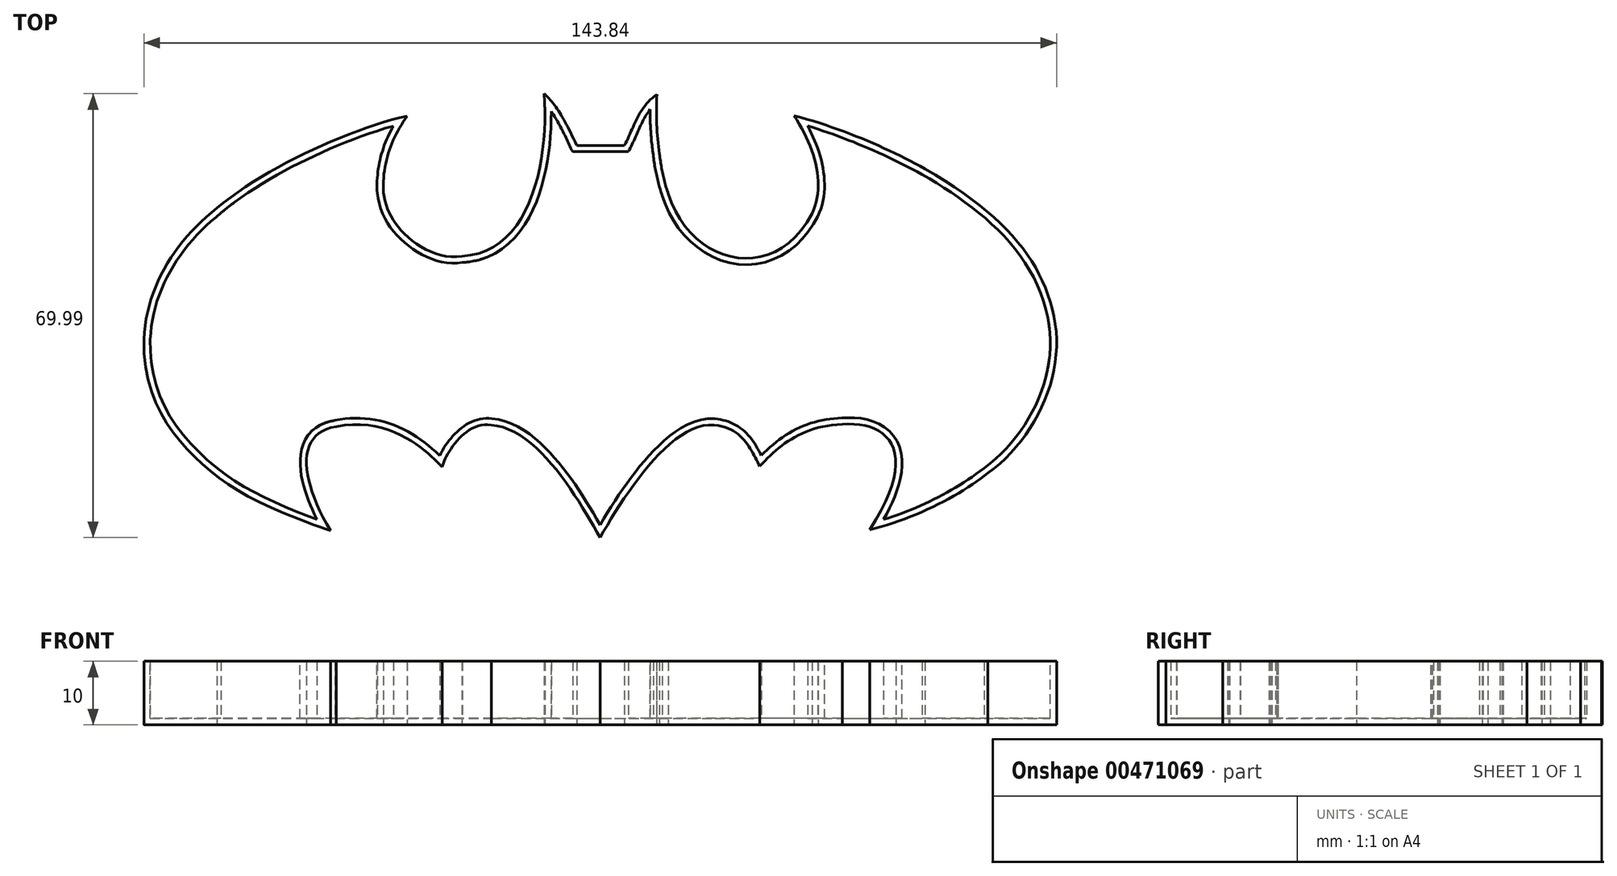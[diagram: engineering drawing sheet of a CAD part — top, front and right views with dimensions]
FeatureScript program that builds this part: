
annotation { "Feature Type Name" : "Feature", "Feature Type Description" : "" }
export const myFeature = defineFeature(function(context is Context, id is Id, definition is map)
    precondition{}
    {
        {
            var Q0;
            Q0=qCreatedBy(makeId("Top.planeOp"),FACE);
            var sketch = newSketch(context, id + "F0", { "sketchPlane" : qUnion([Q0])});
            skLineSegment(sketch, "E0", {"start": v(-3.19, 26.94) * mm, "end": v(4.35, 26.94) * mm});
            skFitSpline(sketch, "E1", {"points": [v(-3.19, 26.94) * mm, v(-8.28, 35.1) * mm], "startDerivative": vector(-5.79, 12.5) * mm, "endDerivative": vector(-5.83, 5.43) * mm});
            skFitSpline(sketch, "E2", {"points": [v(-8.28, 35.1) * mm, v(-21.29, 9.5) * mm], "startDerivative": vector(2.01, -31.97) * mm, "endDerivative": vector(-32.77, -1.6) * mm});
            skFitSpline(sketch, "E3", {"points": [v(-21.29, 9.5) * mm, v(-30.65, 13.35) * mm, v(-33.63, 19.52) * mm], "startDerivative": vector(-19.33, -3.63) * mm, "endDerivative": vector(-2.12, 15.56) * mm});
            skFitSpline(sketch, "E4", {"points": [v(-33.63, 19.52) * mm, v(-29.9, 31.6) * mm], "startDerivative": vector(-0.8, 13.72) * mm, "endDerivative": vector(7.34, 10.53) * mm});
            skFitSpline(sketch, "E5", {"points": [v(-29.9, 31.6) * mm, v(-59.86, 17.08) * mm], "startDerivative": vector(-27.2, -6.27) * mm, "endDerivative": vector(-23.05, -19.48) * mm});
            skFitSpline(sketch, "E6", {"points": [v(-59.86, 17.08) * mm, v(-71.38, -3.61) * mm], "startDerivative": vector(-19.7, -15.69) * mm, "endDerivative": vector(-1.19, -25.13) * mm});
            skFitSpline(sketch, "E7", {"points": [v(-71.38, -3.61) * mm, v(-63.46, -22.06) * mm, v(-41.97, -33.78) * mm], "startDerivative": vector(-1.21, -53.46) * mm, "endDerivative": vector(62.7, -21.26) * mm});
            skFitSpline(sketch, "E8", {"points": [v(-41.97, -33.78) * mm, v(-41.08, -17.39) * mm], "startDerivative": vector(-14.53, 24.29) * mm, "endDerivative": vector(19.35, 2.83) * mm});
            skFitSpline(sketch, "E9", {"points": [v(-41.08, -17.39) * mm, v(-24.7, -23.4) * mm, v(-24.4, -23.76) * mm], "startDerivative": vector(31.3, 6.7) * mm, "endDerivative": vector(-0.55, -1.09) * mm});
            skFitSpline(sketch, "E10", {"points": [v(-24.4, -23.76) * mm, v(-16.64, -17.13) * mm], "startDerivative": vector(1.48, 5.94) * mm, "endDerivative": vector(12.45, -2) * mm});
            skFitSpline(sketch, "E11", {"points": [v(-16.64, -17.13) * mm, v(0.5, -34.88) * mm], "startDerivative": vector(21.55, -1.44) * mm, "endDerivative": vector(11.01, -19.55) * mm});
            skFitSpline(sketch, "E12", {"points": [v(0.5, -34.88) * mm, v(18.52, -17.15) * mm], "startDerivative": vector(12.1, 21.48) * mm, "endDerivative": vector(19.7, -2.01) * mm});
            skFitSpline(sketch, "E13", {"points": [v(18.52, -17.15) * mm, v(25.67, -23.64) * mm], "startDerivative": vector(13.77, -1.3) * mm, "endDerivative": vector(4.03, -7.43) * mm});
            skFitSpline(sketch, "E14", {"points": [v(38.66, -17.02) * mm, v(42.98, -33.64) * mm], "startDerivative": vector(21.92, 1.91) * mm, "endDerivative": vector(-24.23, -36.8) * mm});
            skFitSpline(sketch, "E15", {"points": [v(38.66, -17.02) * mm, v(25.67, -23.64) * mm], "startDerivative": vector(-19.1, -0.7) * mm, "endDerivative": vector(-9.1, -9.92) * mm});
            skFitSpline(sketch, "E16", {"points": [v(42.98, -33.64) * mm, v(61.62, -24.7) * mm], "startDerivative": vector(21.12, 4.96) * mm, "endDerivative": vector(12.58, 10.1) * mm});
            skFitSpline(sketch, "E17", {"points": [v(61.62, -24.7) * mm, v(72.02, 0) * mm], "startDerivative": vector(22.27, 16.03) * mm, "endDerivative": vector(-5.88, 27.35) * mm});
            skFitSpline(sketch, "E18", {"points": [v(72.02, 0) * mm, v(51.73, 23.26) * mm], "startDerivative": vector(-5.63, 26.74) * mm, "endDerivative": vector(-37.9, 22.12) * mm});
            skFitSpline(sketch, "E19", {"points": [v(31.06, 31.66) * mm, v(51.73, 23.26) * mm], "startDerivative": vector(23.83, -6.33) * mm, "endDerivative": vector(17.69, -9.5) * mm});
            skFitSpline(sketch, "E20", {"points": [v(31.06, 31.66) * mm, v(33.92, 16.21) * mm], "startDerivative": vector(10.04, -15.2) * mm, "endDerivative": vector(-6.38, -13.56) * mm});
            skFitSpline(sketch, "E21", {"points": [v(33.92, 16.21) * mm, v(11.26, 19.3) * mm], "startDerivative": vector(-18.02, -34.22) * mm, "endDerivative": vector(-10.37, 33.26) * mm});
            skFitSpline(sketch, "E22", {"points": [v(11.26, 19.3) * mm, v(9.87, 25.6) * mm], "startDerivative": vector(-2.28, 6.45) * mm, "endDerivative": vector(-0.76, 6.45) * mm});
            skFitSpline(sketch, "E23", {"points": [v(9.87, 25.6) * mm, v(9.47, 35) * mm], "startDerivative": vector(-1.34, 9.1) * mm, "endDerivative": vector(0.57, 9.53) * mm});
            skFitSpline(sketch, "E24", {"points": [v(9.47, 35) * mm, v(4.35, 26.94) * mm], "startDerivative": vector(-8.89, -6.11) * mm, "endDerivative": vector(-4.2, -7.9) * mm});
            skCircle(sketch, "E25", {"center": v(0, 0) * mm, "radius": 75.19 * mm});
            skSolve(sketch);
        }
        {
            var Q0;
            Q0=makeQuery(id+"F0.imprint","IMPRINT",FACE,{"disambiguationData":[TD([[makeQuery(id+"F0.imprint","IMPRINT",EDGE,{"derivedFrom":sQuery(id+"F0.wireOp",EDGE,"E0")}),-1.0]])]});
            extrude(context, id + "F1", {"entities" : qUnion([Q0]), "depth" : 10 * mm});
        }
        {
            var Q0;
            Q0=makeQuery(id+"F1.opExtrude","CAP_FACE",FACE,{"disambiguationData":[OSD([sQuery(id+"F0.wireOp",EDGE,"E0"),sQuery(id+"F0.wireOp",EDGE,"E1"),sQuery(id+"F0.wireOp",EDGE,"E2"),sQuery(id+"F0.wireOp",EDGE,"E3"),sQuery(id+"F0.wireOp",EDGE,"E4"),sQuery(id+"F0.wireOp",EDGE,"E5"),sQuery(id+"F0.wireOp",EDGE,"E6"),sQuery(id+"F0.wireOp",EDGE,"E7"),sQuery(id+"F0.wireOp",EDGE,"E8"),sQuery(id+"F0.wireOp",EDGE,"E9"),sQuery(id+"F0.wireOp",EDGE,"E10"),sQuery(id+"F0.wireOp",EDGE,"E11"),sQuery(id+"F0.wireOp",EDGE,"E12"),sQuery(id+"F0.wireOp",EDGE,"E13"),sQuery(id+"F0.wireOp",EDGE,"E14"),sQuery(id+"F0.wireOp",EDGE,"E15"),sQuery(id+"F0.wireOp",EDGE,"E16"),sQuery(id+"F0.wireOp",EDGE,"E17"),sQuery(id+"F0.wireOp",EDGE,"E18"),sQuery(id+"F0.wireOp",EDGE,"E19"),sQuery(id+"F0.wireOp",EDGE,"E20"),sQuery(id+"F0.wireOp",EDGE,"E21"),sQuery(id+"F0.wireOp",EDGE,"E22"),sQuery(id+"F0.wireOp",EDGE,"E23"),sQuery(id+"F0.wireOp",EDGE,"E24")])],"isStart":false});
            shell(context, id + "F2", {"entities" : qUnion([Q0]), "thickness" : 1 * mm});
        }
    });
